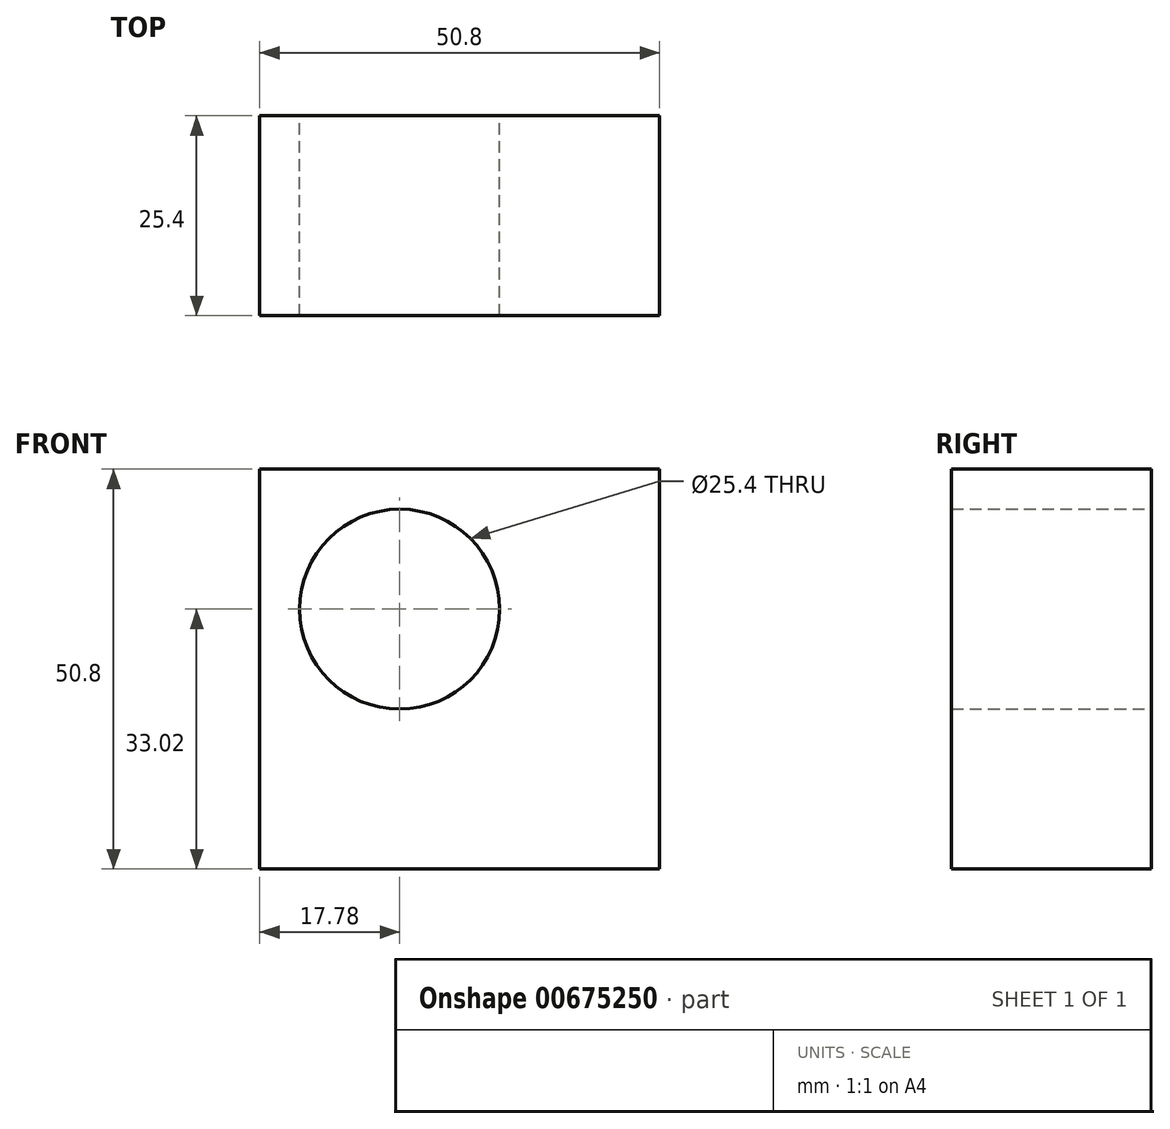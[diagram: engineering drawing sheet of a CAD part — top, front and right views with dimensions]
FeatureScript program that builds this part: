
annotation { "Feature Type Name" : "Feature", "Feature Type Description" : "" }
export const myFeature = defineFeature(function(context is Context, id is Id, definition is map)
    precondition{}
    {
        {
            var Q0;
            Q0=qCreatedBy(makeId("Front.planeOp"),FACE);
            var sketch = newSketch(context, id + "F0", { "sketchPlane" : qUnion([Q0])});
            skLineSegment(sketch, "E0.bottom", {"start": v(0, 0) * mm, "end": v(50.8, 0) * mm});
            skLineSegment(sketch, "E0.top", {"start": v(0, 50.8) * mm, "end": v(50.8, 50.8) * mm});
            skLineSegment(sketch, "E0.left", {"start": v(0, 0) * mm, "end": v(0, 50.8) * mm});
            skLineSegment(sketch, "E0.right", {"start": v(50.8, 0) * mm, "end": v(50.8, 50.8) * mm});
            skCircle(sketch, "E1", {"center": v(17.78, 33.02) * mm, "radius": 12.7 * mm});
            skSolve(sketch);
        }
        {
            var Q0;
            Q0=makeQuery(id+"F0.imprint","IMPRINT",FACE,{"disambiguationData":[TD([[makeQuery(id+"F0.imprint","IMPRINT",EDGE,{"derivedFrom":sQuery(id+"F0.wireOp",EDGE,"E0.bottom")}),1.0]])]});
            extrude(context, id + "F1", {"entities" : qUnion([Q0]), "depth" : 25.4 * mm, "offsetDistance" : 25.4 * mm});
        }
    });
